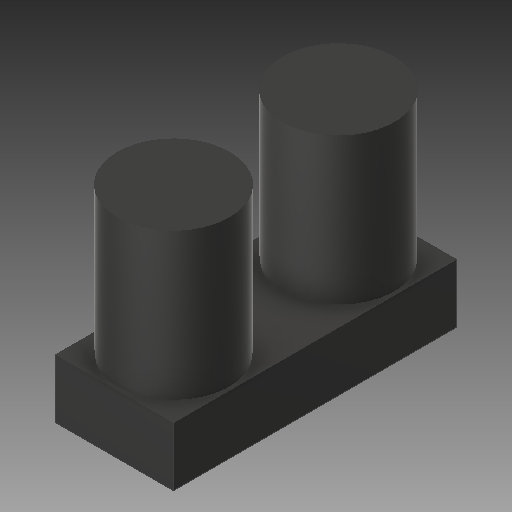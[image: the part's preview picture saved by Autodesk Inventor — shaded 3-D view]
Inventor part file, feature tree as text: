
AUTODESK INVENTOR PART (.ipt)
format: ipt  version: 2018 (Build 220112000, 112)  size: 121,344 bytes
history: native  units: mm
features: extrude x4, sketch x1
ambient origin geometry x8: Origin, YZ Plane, XZ Plane, XY Plane, X Axis, Y Axis, Z Axis, Center Point
bodies: Solid1 (feature_tree)
feature tree (5):
  sketch  "Sketch1"  dims[d0=20.0mm d1=48.0mm d2=23.5mm d3=9.5mm d4=19.0mm d5=23.5mm d6=9.5mm d7=19.0mm d8=25.0mm d9=0.0mm d10=10.0mm d11=0.0mm d12=10.0mm d13=0.0mm d14=10.0mm d15=0.0mm]
  extrude  "Extrusion1"  Depth=48.0mm
  extrude  "Extrusion2"  Depth=10.0mm
  extrude  "Extrusion3"  Depth=9.5mm
  extrude  "Extrusion4"  Depth=10.0mm
